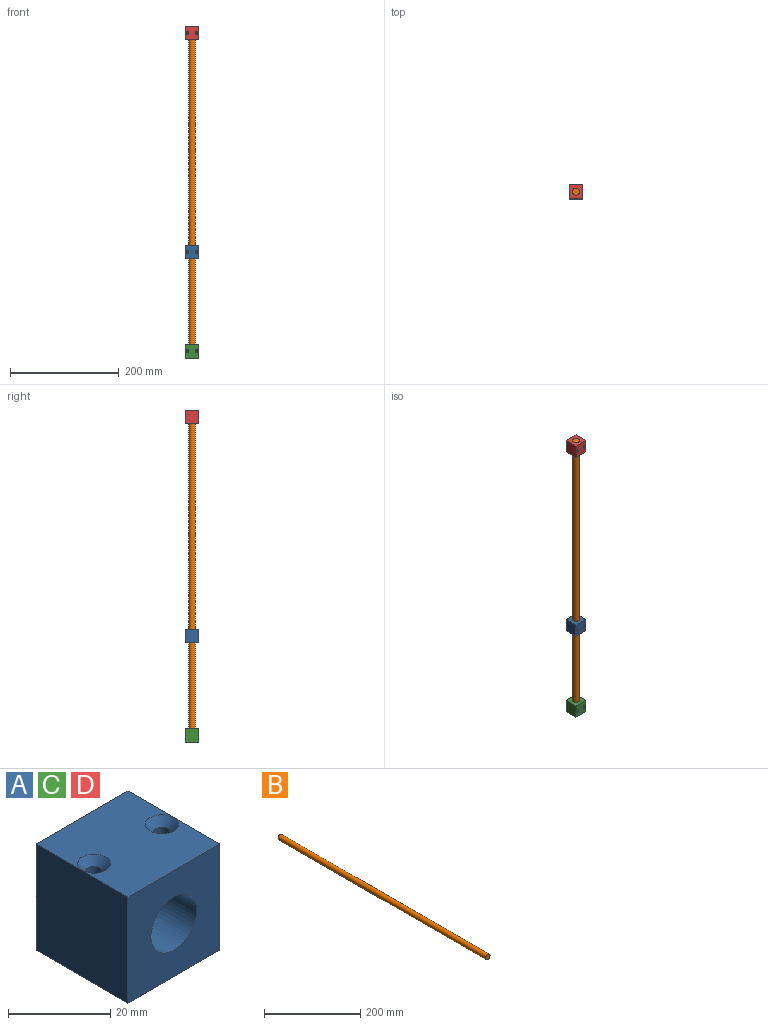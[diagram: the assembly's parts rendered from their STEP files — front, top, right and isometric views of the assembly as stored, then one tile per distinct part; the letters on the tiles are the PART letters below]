
ASSEMBLY  parts=4 mates=3
PART A: 11 faces, bbox 25.4x25.4x25.4 mm
  f0: plane 25.4x25.4mm, normal (-1,0,0), area 645.2mm2, adj f1,f4,f5,f6
  f1: plane 25.4x25.4mm, normal (0,0,-1), area 628.4mm2, adj f0,f2,f5,f6,f7,f9
  f2: plane 25.4x25.4mm, normal (1,0,0), area 645.2mm2, adj f1,f4,f5,f6
  f3: cylinder r=6.35mm len=25.4mm, axis (0,1,0), area 1013.4mm2, adj f5,f6
  f4: plane 25.4x25.4mm, normal (0,0,1), area 579.3mm2, adj f0,f2,f5,f6,f8,f10
  f5: plane 25.4x25.4mm, normal (0,-1,0), area 518.5mm2, adj f0,f1,f2,f3,f4
  f6: plane 25.4x25.4mm, normal (0,1,0), area 518.5mm2, adj f0,f1,f2,f3,f4
  f7: cylinder r=1.63mm len=23.55mm, axis (0,0,1), area 241.5mm2, adj f1,f8
  f8: cone r=1.63mm half-angle=41deg, axis (0,0,1), area 37.5mm2, adj f4,f7
  f9: cylinder r=1.63mm len=23.55mm, axis (0,0,1), area 241.5mm2, adj f1,f10
  f10: cone r=1.63mm half-angle=41deg, axis (0,0,1), area 37.5mm2, adj f4,f9
PART B: 3 faces, bbox 12.7x609.6x12.7 mm
  f0: cylinder r=6.35mm len=609.6mm, axis (0,-1,0), area 24322mm2, adj f1,f2
  f1: plane 12.7x12.7mm, normal (0,1,0), area 126.7mm2, adj f0
  f2: plane 12.7x12.7mm, normal (0,-1,0), area 126.7mm2, adj f0
PART C: same geometry as A
PART D: same geometry as A
PLACE A rot(axis=(0,-0.71,0.71),180deg) t=(-50.28,-0.91,-133.59)mm
PLACE B rot(axis=(1,0,0),90deg) t=(51.32,-0.91,-315.62)mm
PLACE C rot(axis=(0,0.71,-0.71),180deg) t=(-50.28,-0.91,-315.62)mm fixed
PLACE D rot(axis=(1,0,0),90deg) t=(51.32,-0.91,293.98)mm
MATE slider A.f3 <-> B.f0  axis (0,0,1) through (0.52,-0.91,-108.19)mm
MATE fastened C.f3 <-> B.f0  axis (0,0,-1) through (0.52,-0.91,-315.62)mm
MATE fastened D.f3 <-> B.f0  axis (0,0,1) through (0.52,-0.91,293.98)mm
